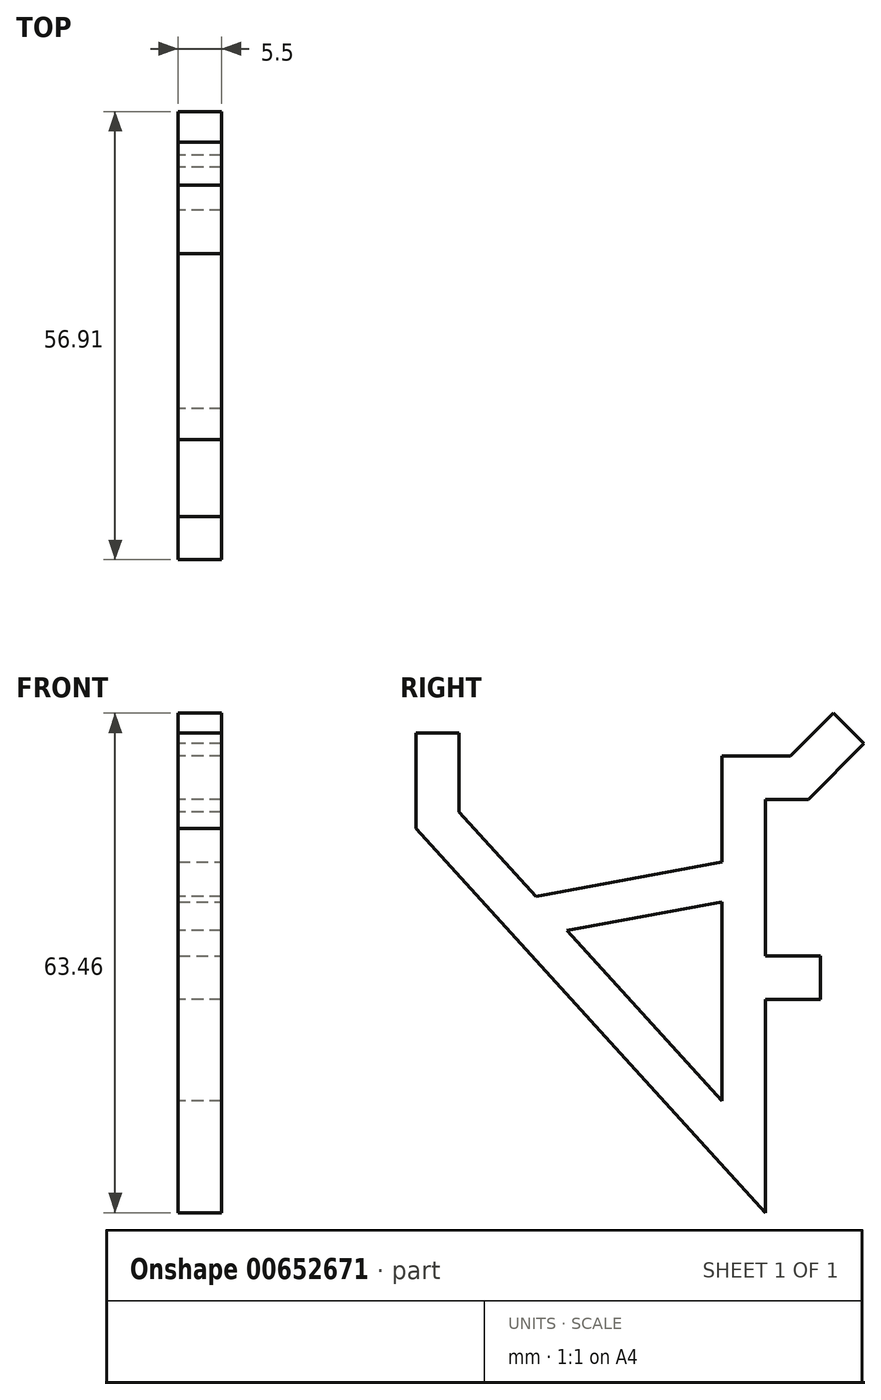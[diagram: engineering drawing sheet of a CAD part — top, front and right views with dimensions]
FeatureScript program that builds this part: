
annotation { "Feature Type Name" : "Feature", "Feature Type Description" : "" }
export const myFeature = defineFeature(function(context is Context, id is Id, definition is map)
    precondition{}
    {
        {
            var Q0;
            Q0=qCreatedBy(makeId("Front.planeOp"),FACE);
            var sketch = newSketch(context, id + "F0", { "sketchPlane" : qUnion([Q0])});
            skLineSegment(sketch, "E0", {"start": v(0, 0) * mm, "end": v(0, 25.4) * mm});
            skCircle(sketch, "E1", {"center": v(0, 25.4) * mm, "radius": 3.97 * mm});
            skCircle(sketch, "E2", {"center": v(0, 0) * mm, "radius": 3.97 * mm});
            skLineSegment(sketch, "E3.bottom", {"start": v(-2.8, 28.2) * mm, "end": v(2.8, 28.2) * mm});
            skLineSegment(sketch, "E3.top", {"start": v(-2.8, 22.6) * mm, "end": v(2.8, 22.6) * mm});
            skLineSegment(sketch, "E3.left", {"start": v(-2.8, 28.2) * mm, "end": v(-2.8, 22.6) * mm});
            skLineSegment(sketch, "E3.right", {"start": v(2.8, 28.2) * mm, "end": v(2.8, 22.6) * mm});
            skSolve(sketch);
        }
        {
            var Q0;
            Q0=qCreatedBy(makeId("Front.planeOp"),FACE);
            var sketch = newSketch(context, id + "F1", { "sketchPlane" : qUnion([Q0])});
            skLineSegment(sketch, "E4.bottom", {"start": v(2.75, 2.75) * mm, "end": v(-2.75, 2.75) * mm});
            skLineSegment(sketch, "E4.top", {"start": v(2.75, -2.75) * mm, "end": v(-2.75, -2.75) * mm});
            skLineSegment(sketch, "E4.left", {"start": v(2.75, 2.75) * mm, "end": v(2.75, -2.75) * mm});
            skLineSegment(sketch, "E4.right", {"start": v(-2.75, 2.75) * mm, "end": v(-2.75, -2.75) * mm});
            skPoint(sketch, "E4.middle", {"position": v(0, 0) * mm});
            skSolve(sketch);
        }
        {
            var Q0;
            Q0 = qSketchRegion(id + "F1", true);
            extrude(context, id + "F2", {"entities" : qUnion([Q0]), "oppositeDirection" : true, "depth" : 7 * mm, "offsetDistance" : 25 * mm, "hasSecondDirection" : true, "secondDirectionOppositeDirection" : false, "secondDirectionDepth" : 5.5 * mm});
        }
        {
            var Q0;
            Q0=qCreatedBy(makeId("Front.planeOp"),FACE);
            var sketch = newSketch(context, id + "F3", { "sketchPlane" : qUnion([Q0])});
            skLineSegment(sketch, "E5.bottom", {"start": v(2.75, 22.65) * mm, "end": v(-2.75, 22.65) * mm});
            skLineSegment(sketch, "E5.top", {"start": v(2.75, 28.15) * mm, "end": v(-2.75, 28.15) * mm});
            skLineSegment(sketch, "E5.left", {"start": v(2.75, 22.65) * mm, "end": v(2.75, 28.15) * mm});
            skLineSegment(sketch, "E5.right", {"start": v(-2.75, 22.65) * mm, "end": v(-2.75, 28.15) * mm});
            skPoint(sketch, "E5.middle", {"position": v(0, 25.4) * mm});
            skSolve(sketch);
        }
        {
            var Q0;
            Q0 = qSketchRegion(id + "F3", true);
            var Q1;
            Q1=makeQuery(id+"F2.opExtrude","CAP_FACE",FACE,{"disambiguationData":[OSD([sQuery(id+"F1.wireOp",EDGE,"E4.bottom"),sQuery(id+"F1.wireOp",EDGE,"E4.top"),sQuery(id+"F1.wireOp",EDGE,"E4.left"),sQuery(id+"F1.wireOp",EDGE,"E4.right")])],"isStart":true});
            extrude(context, id + "F4", {"entities" : qUnion([Q0]), "endBound" : BoundingType.UP_TO_SURFACE, "depth" : 25 * mm, "endBoundEntityFace" : qUnion([Q1]), "offsetDistance" : 25 * mm});
        }
        {
            var Q0;
            Q0=makeQuery(id+"F2.opExtrude","SWEPT_FACE",FACE,{"disambiguationData":[OSD([sQuery(id+"F1.wireOp",EDGE,"E4.bottom")])]});
            var sketch = newSketch(context, id + "F5", { "sketchPlane" : qUnion([Q0])});
            skLineSegment(sketch, "E6.bottom", {"start": v(-2.75, -5.5) * mm, "end": v(2.75, -5.5) * mm});
            skLineSegment(sketch, "E6.top", {"start": v(-2.75, 0) * mm, "end": v(2.75, 0) * mm});
            skLineSegment(sketch, "E6.left", {"start": v(-2.75, -5.5) * mm, "end": v(-2.75, 0) * mm});
            skLineSegment(sketch, "E6.right", {"start": v(2.75, -5.5) * mm, "end": v(2.75, 0) * mm});
            skSolve(sketch);
        }
        {
            var Q0;
            Q0 = qSketchRegion(id + "F5", true);
            var Q1;
            Q1=makeQuery(id+"F4.opExtrude","SWEPT_FACE",FACE,{"disambiguationData":[OSD([sQuery(id+"F3.wireOp",EDGE,"E5.bottom")])]});
            extrude(context, id + "F6", {"entities" : qUnion([Q0]), "operationType" : NewBodyOperationType.ADD, "endBound" : BoundingType.UP_TO_SURFACE, "depth" : 25 * mm, "endBoundEntityFace" : qUnion([Q1]), "offsetDistance" : 25 * mm});
        }
        {
            var Q0;
            Q0=qCreatedBy(makeId("Right.planeOp"),FACE);
            var sketch = newSketch(context, id + "F7", { "sketchPlane" : qUnion([Q0])});
            skLineSegment(sketch, "E7", {"start": v(0, 28.15) * mm, "end": v(3.18, 28.15) * mm});
            skLineSegment(sketch, "E8", {"start": v(3.17, 28.15) * mm, "end": v(8.64, 33.61) * mm});
            skLineSegment(sketch, "E9", {"start": v(8.64, 33.61) * mm, "end": v(12.52, 29.72) * mm});
            skLineSegment(sketch, "E10", {"start": v(12.52, 29.72) * mm, "end": v(5.45, 22.65) * mm});
            skLineSegment(sketch, "E11", {"start": v(5.45, 22.65) * mm, "end": v(0, 22.65) * mm});
            skLineSegment(sketch, "E12", {"start": v(0, 22.65) * mm, "end": v(0, 28.15) * mm});
            skSolve(sketch);
        }
        {
            var Q0;
            Q0 = qSketchRegion(id + "F7", true);
            var Q1;
            Q1=makeQuery(id+"F6.boolean.opBoolean","MERGE",FACE,{"derivedFrom":[makeQuery(id+"F2.opExtrude","SWEPT_FACE",FACE,{"disambiguationData":[OSD([sQuery(id+"F1.wireOp",EDGE,"E4.left")])]}),makeQuery(id+"F4.opExtrude","SWEPT_FACE",FACE,{"disambiguationData":[OSD([sQuery(id+"F3.wireOp",EDGE,"E5.left")])]}),makeQuery(id+"F6.opExtrude","SWEPT_FACE",FACE,{"disambiguationData":[OSD([sQuery(id+"F5.wireOp",EDGE,"E6.right")])]})]});
            var Q2;
            Q2=makeQuery(id+"F6.boolean.opBoolean","MERGE",FACE,{"derivedFrom":[makeQuery(id+"F2.opExtrude","SWEPT_FACE",FACE,{"disambiguationData":[OSD([sQuery(id+"F1.wireOp",EDGE,"E4.right")])]}),makeQuery(id+"F4.opExtrude","SWEPT_FACE",FACE,{"disambiguationData":[OSD([sQuery(id+"F3.wireOp",EDGE,"E5.right")])]}),makeQuery(id+"F6.opExtrude","SWEPT_FACE",FACE,{"disambiguationData":[OSD([sQuery(id+"F5.wireOp",EDGE,"E6.left")])]})]});
            extrude(context, id + "F8", {"entities" : qUnion([Q0]), "operationType" : NewBodyOperationType.ADD, "endBound" : BoundingType.UP_TO_SURFACE, "depth" : 25 * mm, "endBoundEntityFace" : qUnion([Q1]), "offsetDistance" : 25 * mm, "hasSecondDirection" : true, "secondDirectionBound" : SecondDirectionBoundingType.UP_TO_SURFACE, "secondDirectionOppositeDirection" : true, "secondDirectionDepth" : 25 * mm, "secondDirectionBoundEntityFace" : qUnion([Q2])});
        }
        {
            var Q0;
            Q0=qCreatedBy(makeId("Right.planeOp"),FACE);
            var sketch = newSketch(context, id + "F9", { "sketchPlane" : qUnion([Q0])});
            skLineSegment(sketch, "E13", {"start": v(0, 0) * mm, "end": v(0, -29.85) * mm});
            skLineSegment(sketch, "E14", {"start": v(0, -29.85) * mm, "end": v(-44.4, 18.93) * mm});
            skLineSegment(sketch, "E15", {"start": v(-44.4, 18.93) * mm, "end": v(-44.4, 31.09) * mm});
            skLineSegment(sketch, "E16", {"start": v(-44.4, 31.09) * mm, "end": v(-38.9, 31.09) * mm});
            skLineSegment(sketch, "E17", {"start": v(-38.9, 31.09) * mm, "end": v(-38.9, 21.06) * mm});
            skLineSegment(sketch, "E18", {"start": v(-38.9, 21.06) * mm, "end": v(-5.5, -15.63) * mm});
            skLineSegment(sketch, "E19", {"start": v(-5.5, -15.63) * mm, "end": v(-5.5, 0) * mm});
            skLineSegment(sketch, "E20", {"start": v(0, 0) * mm, "end": v(-5.5, 0) * mm});
            skLineSegment(sketch, "E21", {"start": v(-5.38, 14.76) * mm, "end": v(-29.14, 10.34) * mm});
            skLineSegment(sketch, "E22.0", {"start": v(-4.46, 9.84) * mm, "end": v(-28.23, 5.42) * mm});
            skLineSegment(sketch, "E23", {"start": v(-29.14, 10.34) * mm, "end": v(-28.23, 5.42) * mm});
            skLineSegment(sketch, "E24", {"start": v(-5.38, 14.76) * mm, "end": v(-4.46, 9.84) * mm});
            skSolve(sketch);
        }
        {
            var Q0;
            Q0 = qSketchRegion(id + "F9", true);
            extrude(context, id + "F10", {"entities" : qUnion([Q0]), "operationType" : NewBodyOperationType.ADD, "endBound" : BoundingType.SYMMETRIC, "depth" : 5.5 * mm, "offsetDistance" : 25 * mm});
        }
    });
